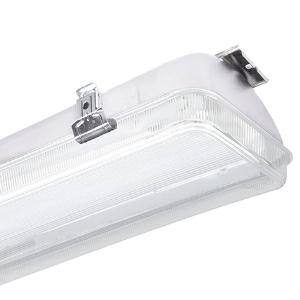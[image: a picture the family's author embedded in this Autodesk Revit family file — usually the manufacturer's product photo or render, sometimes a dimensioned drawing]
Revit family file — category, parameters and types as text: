
# Revit family: 3f_filippi_-_beta_235_75_pc_ampio_3f_filippi_-_52931_-_beta_235_led_751x25_ampio_l655
name_source: partatom
category: Lighting Fixtures
units: mm (PartAtom-declared; Revit-internal decimal feet)

## family parameters
Cut with Voids When Loaded = No
Host = Face
Light Source = No
Part Type = Normal
Room Calculation Point = No
Round Connector Dimension = Use Diameter
Shared = No

## types (1)
- 3F Filippi - Beta 235 75 PC Ampio (1 x LED, 4143 lm, 27.5 W, 4000 K)
    Apparent Load = 28 VA
    Approval mark = CE
    CIE Flux Codes = 60 88 98 97 100
    Color Rendering = 80
    Color Temperature = 4000 K
    Control Gear = Electronic ballast
    Default Elevation = 1800 mm
    Description = ILLUMINOTECHNICAL
Luminous efficiency 100% (DLOR 99%, ULOR 1%).
Initial luminous flux of the luminaire 4143 lm.
Wide symmetric distribution.
Installation Interdistance Transv.D = 1.25 x hu - Long.D = 1.44 x hu.
Tabular UGR (CIE 117 - 4H-8H; S=0.25H; 70/50/20): RUG 19.2 - 19.7.
Beam angle: 91° - 102°.
Luminous efficacy 151 lm/W.
Lifetime (L93/B10): 30000 h. (tq+25°C)
Lifetime (L90/B10): 50000 h. (tq+25°C)
Lifetime (L85/B10): 80000 h. (tq+25°C)
Lifetime (L80/B10): 100000 h. (tq+25°C)
Lifetime (L85/B10): 50000 h. (tq+45°C)
Sudden decreased luminous flux after 50000 hours: 0% (C0).
Photobiological safety in compliance with IEC/TR 62778: RG0 risk exempt, (IEC 62471).
In compliance with IEC/EN 62722-2-1 - IEC/EN 62717 standards.

SOURCE
Linear LED module 25W/840.
Energy efficiency class (UE 2019/2020 - UE 2019/2015): C.
CIE 13.3 Colour rendering index: CRI >80 (R9 <50%).
IES TM-30 Fidelity Index: Rf = 84 Rg = 95.
CCT nominal colour temperature 4000 K.
Colour initial tolerance (MacAdam): SDCM 3.

MECHANICAL
Single-piece housing in pressed steel, powder-coated in white epoxy-polyester.
Polycarbonate screen etched internally, V2 self-extinguishing, UV stabilised, injection moulded.
Ecologic anti-aging injected sealing gasket.
Oversized gear-tray reflector unit in highly reflective white painted hot-galvanised steel.
Methacrylate (PMMA) lenses with external flat surface.
Galvanised steel safety snap-lock clips for diffuser mounting.
Luminaire with limited surface temperature. - D - (EN 60598-2-24)
Dimensions: 655x235 mm, height 140 mm. Weight 3.815 kg.
IP65 protection degree.
Mechanical strength to impacts IK10 (20 joule).
Glow-wire test resistance 850°C.

ELECTRICAL
Halogen Free electronic wiring 230V-50/60Hz, power factor 0.90, THD <25%, constant output current, class I, 1 driver.
Power of the luminaire 27.5 W.
ENEC - CE.
Flicker: <4%.
Luminaire compliant with EN 60598-2-22 for power supply from a centralised emergency system CPSS (Central Power Supply System), not incorporated in the luminaire - high risk areas excluded. The default power and flux are 100% in AC and 100% in DC.
Ambient temperature from -20°C to +45°C.
Temperature class T6 max 85°C.
Quick connection via M20 3P connector with 9-13 mm tightening range.
Relative humidity UR: <85%.

INSTALLATION
Ceiling / Suspended / Wall.
All accessories dedicated to this product are available on the Catalog and on our website www.3F-Filippi.com.

APPLICATIONS
Suitable product for food production plants (HACCP), IFS (Food Version 6), BRC (GSFS Food Version 7).
Dry, dusty indoor environments, subject to occasional water splashes.
Industrial environments, warehouses, environments where security locks are required on all clips, e.g. prisons.
Environments in which it is necessary a total protection against falling fragments (eg environments with foodstuffs or machines with moving parts or with extreme temperature changes), use luminaires with laminated glass.
Tempered glass is not immune to falling fragments from harmless and caused by shocks or exceptionally derived from the tempering process.

WARNING
Fixture not suitable for cold stores with an ambient temperature <0°C and/or relative humidity >85%.
Luminaire designed for disposal/recycling at end-of-life.
Replaceable (LED only) light source by a professional. Replaceable control gear by a professional.
    Height = 140 mm  [stored 0.459318 ft]
    Lamp = 1 x LED
    Lamp Light Flux = 4143 lm
    Lamp Power = 27.5 W
    Lamp count = 1
    Length = 655 mm
    Lifetime = 50000 h
    Luminous efficacy = 151 lm/W
    Manufacturer = 3F Filippi
    ModVariant = No
    Model = 3F Filippi - 52931 - Beta 235 LED 751x25 AMPIO L655
    Mounting Place = Ceiling
    Mounting Type = Pendant
    Number of Poles = 1
    OnlyDefault = Yes
    Power Factor = 1
    Product Name = 3F Filippi - Beta 235 75 PC Ampio
    Product group = pendant luminaire
    ProductGroupID = 9
    Protection Class = Protection class I
    Protection Degree = IP 65
    RLX_Detail_Level = 1
    RLX_Emergency_Light_Flux = 0 lm
    RLX_Emergency_Type = 0
    RLX_Emergency_Type_DB = No
    RlxData = <blob elided: 87405 chars, md5=4ced7694>
    Socket = socket
    Standby Power = 0 W
    System Light Flux = 4143 lm
    System Power = 28 W
    Type Comments = Product without accessories
    Type Image = 3ffilippi_52931.jpg
    URL = http://relux.com
    VarID = ---
    Voltage = 0 V
    Weight = 0.00 kg
    Width = 235 mm

note: [stored X ft] marks values corroborated as IEEE doubles in the binary element streams (Revit-internal decimal feet)

## geometry (parser evidence)
native form markers: Blend x4, Sweep x10
no freeform markers — native parametric forms only
